# Revit family: Reece_Sink_Posh_Solus_Inset or Undermount Sink_Single Bowl_Round_1 Taphole
name_source: partatom
category: Plumbing Fixtures
revit_build: Autodesk Revit 2018 (Build: 20180329_1100(x64)
units: mm (PartAtom-declared; Revit-internal decimal feet)

## family parameters
Cut with Voids When Loaded = No
Host = Face
Part Type = Normal
Room Calculation Point = Yes
Round Connector Dimension = Use Diameter
Shared = Yes

## types (1)
- 1 Taphole_500mm_Stainless Steel
    CWFU = 0
    Default Elevation = 0 mm  [stored 0 ft]
    Description = Single Bowl
    Disclaimer = THIS FILE IS THE PROPERTY OF THE REECE GROUP. IT MAY NOT BE REPRODUCED, REVERSE-ENGINEERED OR MODIFIED. ANY REPUBLICATION, TRANSMISSION OR DISTRIBUTION FOR THE PURPOSE OF COMMERCIALLY EXPLOITING THE FILES IS PROHIBITED.
    HWFU = 0
    Keynote = Product #9508918, Reece_Sink_Posh_Solus_Inset or Undermount Sink_Single Bowl_Round_1 Taphole - 1 Taphole_500mm_Stainless Steel
    Manufacturer = Posh
    Model = Solus
    Reece_Detail_Additional = No Overflow
    Reece_Detail_Connector = 1 Taphole
    Reece_Detail_Disclaimer = THIS FILE IS THE PROPERTY OF THE REECE GROUP. IT MAY NOT BE REPRODUCED, REVERSE-ENGINEERED OR MODIFIED. ANY REPUBLICATION, TRANSMISSION OR DISTRIBUTION FOR THE PURPOSE OF COMMERCIALLY EXPLOITING THE FILES IS PROHIBITED.
    Reece_Detail_Installation = Inset/ Undermount
    Reece_Material_Main = Reece_Metal_Steel
    Reece_Material_Secondary = Reece_Metal_Steel
    Reece_Overall_Capacity = 16 L
    Reece_Overall_Height = 170 mm
    Reece_Overall_Length = 505 mm  [stored 1.65682 ft]
    Reece_Overall_Width = 505 mm  [stored 1.65682 ft]
    Reece_Product_Brand = Posh
    Reece_Product_Description = Posh Solus Round Inset/Undermount Sink 1 Taphole 500mm Stainless Steel
    Reece_Product_Mount = Inset / Undermount
    Reece_Product_Number = 9508918
    Reece_Product_Sub Brand = Solus
    Reece_Product_Type = Undermount Sink
    Reece_Product_Web Page = https://www.reece.com.au
    Reece_Sink_Lip Thickness = 6 mm  [stored 0.019685 ft]
    Reece_Sink_Outlet = 40 mm  [stored 0.131234 ft]
    Reece_Sink_Type = 1 Taphole_No Drainer_Stainless Steel : No Taphole_No Drainer_Stainless Steel
    Type Comments = Undermount Sink
    URL = https://www.reece.com.au
    WFU = 0

note: [stored X ft] marks values corroborated as IEEE doubles in the binary element streams (Revit-internal decimal feet)

## geometry (parser evidence)
native form markers: Sweep x3
no freeform markers — native parametric forms only
